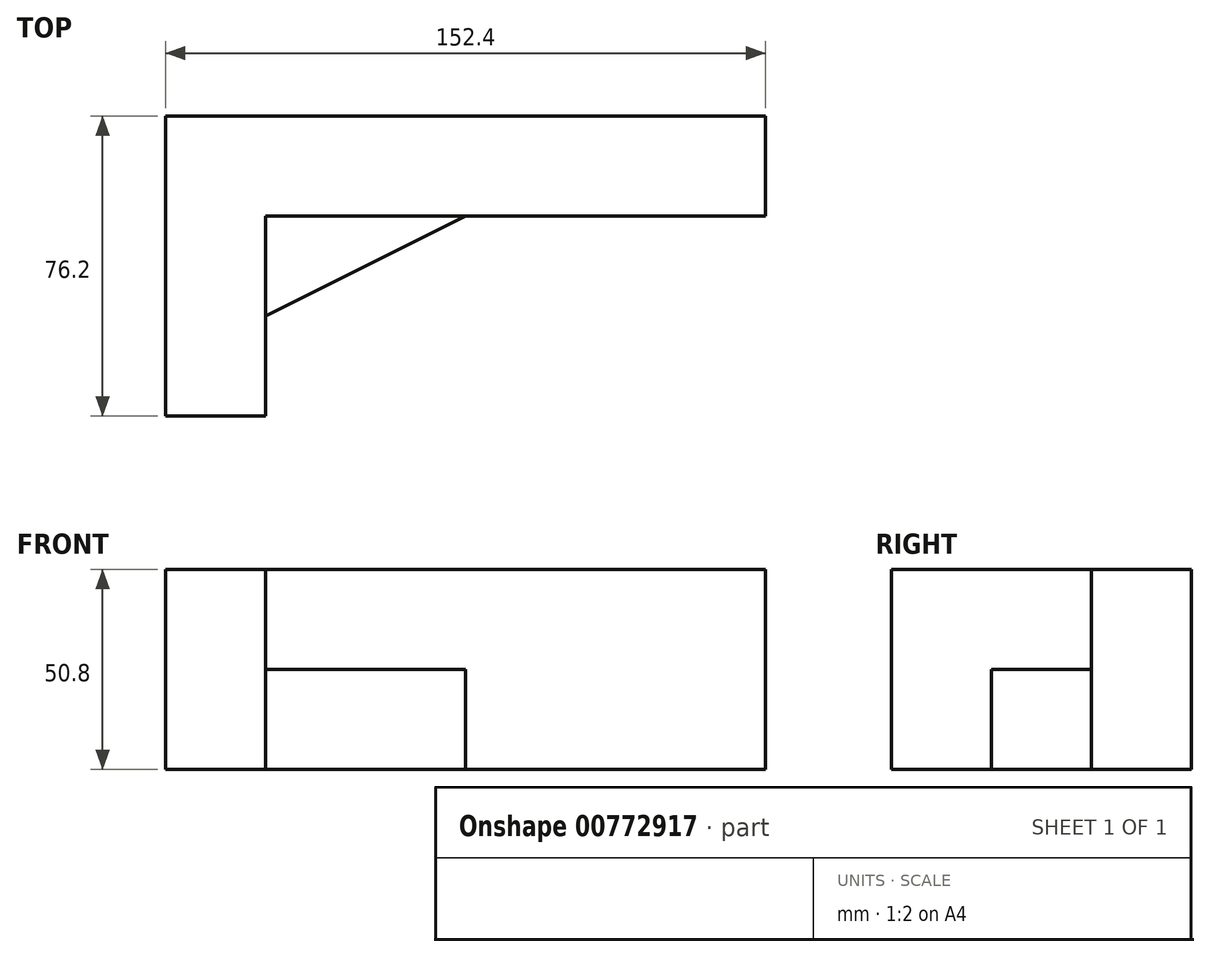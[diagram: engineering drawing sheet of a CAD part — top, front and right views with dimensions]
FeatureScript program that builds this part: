
annotation { "Feature Type Name" : "Feature", "Feature Type Description" : "" }
export const myFeature = defineFeature(function(context is Context, id is Id, definition is map)
    precondition{}
    {
        {
            var Q0;
            Q0=qCreatedBy(makeId("Front.planeOp"),FACE);
            var sketch = newSketch(context, id + "F0", { "sketchPlane" : qUnion([Q0])});
            skLineSegment(sketch, "E0", {"start": v(0, 0) * mm, "end": v(152.4, 0) * mm});
            skLineSegment(sketch, "E1", {"start": v(152.4, 0) * mm, "end": v(152.4, 50.8) * mm});
            skLineSegment(sketch, "E2", {"start": v(152.4, 50.8) * mm, "end": v(0, 50.8) * mm});
            skLineSegment(sketch, "E3", {"start": v(0, 50.8) * mm, "end": v(0, 0) * mm});
            skSolve(sketch);
        }
        {
            var Q0;
            Q0=makeQuery(id+"F0.imprint","IMPRINT",FACE,{"disambiguationData":[TD([[makeQuery(id+"F0.imprint","IMPRINT",EDGE,{"derivedFrom":sQuery(id+"F0.wireOp",EDGE,"E0")}),1.0]])]});
            extrude(context, id + "F1", {"entities" : qUnion([Q0]), "depth" : 76.2 * mm, "offsetDistance" : 25.4 * mm});
        }
        {
            var Q0;
            Q0=makeQuery(id+"F1.opExtrude","SWEPT_FACE",FACE,{"disambiguationData":[OSD([sQuery(id+"F0.wireOp",EDGE,"E2")])]});
            var sketch = newSketch(context, id + "F2", { "sketchPlane" : qUnion([Q0])});
            skLineSegment(sketch, "E4", {"start": v(0, -76.2) * mm, "end": v(25.4, -76.2) * mm});
            skLineSegment(sketch, "E5", {"start": v(25.4, -76.2) * mm, "end": v(25.4, -25.4) * mm});
            skLineSegment(sketch, "E6", {"start": v(25.4, -25.4) * mm, "end": v(152.4, -25.4) * mm});
            skSolve(sketch);
        }
        {
            var Q0;
            {var subQ0=sQuery(id+"F2.wireOp",EDGE,"E5");Q0=makeQuery(id+"F2.imprint","IMPRINT",FACE,{"disambiguationData":[TD([[makeQuery(id+"F2.imprint","IMPRINT",EDGE,{"derivedFrom":subQ0}),-1.0]])]});}
            extrude(context, id + "F3", {"entities" : qUnion([Q0]), "operationType" : NewBodyOperationType.REMOVE, "oppositeDirection" : true, "depth" : 25.4 * mm, "offsetDistance" : 25.4 * mm});
        }
        {
            var Q0;
            Q0=makeQuery(id+"F3.boolean.opBoolean","COPY",FACE,{"derivedFrom":makeQuery(id+"F3.opExtrude","CAP_FACE",FACE,{"disambiguationData":[OSD([sQuery(id+"F0.wireOp",EDGE,"E1"),sQuery(id+"F0.wireOp",EDGE,"E2"),sQuery(id+"F2.wireOp",EDGE,"E5"),sQuery(id+"F2.wireOp",EDGE,"E6")])],"isStart":false})});
            var sketch = newSketch(context, id + "F4", { "sketchPlane" : qUnion([Q0])});
            skLineSegment(sketch, "E7", {"start": v(25.4, -76.2) * mm, "end": v(25.4, -50.8) * mm});
            skLineSegment(sketch, "E8", {"start": v(152.4, -25.4) * mm, "end": v(76.2, -25.4) * mm});
            skLineSegment(sketch, "E9", {"start": v(76.2, -25.4) * mm, "end": v(25.4, -50.8) * mm});
            skSolve(sketch);
        }
        {
            var Q0;
            Q0=makeQuery(id+"F4.imprint","IMPRINT",FACE,{"disambiguationData":[TD([[makeQuery(id+"F4.imprint","IMPRINT",EDGE,{"derivedFrom":sQuery(id+"F4.wireOp",EDGE,"E7")}),-1.0]])]});
            extrude(context, id + "F5", {"entities" : qUnion([Q0]), "operationType" : NewBodyOperationType.REMOVE, "oppositeDirection" : true, "depth" : 25.4 * mm, "offsetDistance" : 25.4 * mm});
        }
    });
